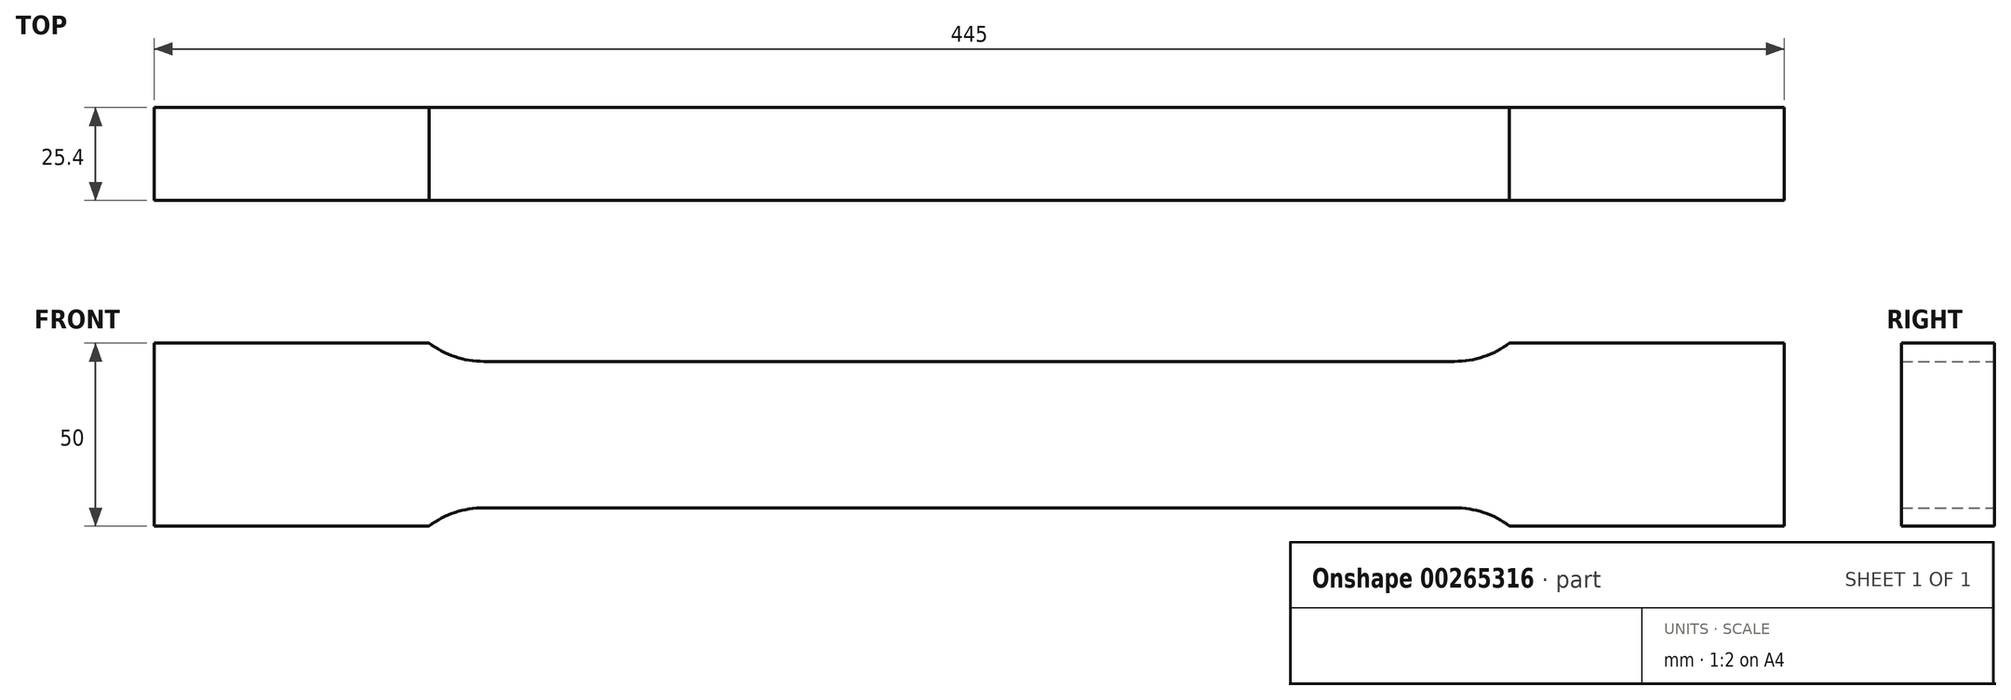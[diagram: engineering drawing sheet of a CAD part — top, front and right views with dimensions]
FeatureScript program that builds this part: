
annotation { "Feature Type Name" : "Feature", "Feature Type Description" : "" }
export const myFeature = defineFeature(function(context is Context, id is Id, definition is map)
    precondition{}
    {
        {
            var Q0;
            Q0=qCreatedBy(makeId("Front.planeOp"),FACE);
            var sketch = newSketch(context, id + "F0", { "sketchPlane" : qUnion([Q0])});
            skLineSegment(sketch, "E0", {"start": v(0, 20) * mm, "end": v(132.5, 20) * mm});
            skArc(sketch, "E1", {"start": v(132.5, 20) * mm, "mid": v(140.4, 21.28) * mm, "end": v(147.5, 25) * mm});
            skLineSegment(sketch, "E2", {"start": v(147.5, 25) * mm, "end": v(222.5, 25) * mm});
            skLineSegment(sketch, "E3", {"start": v(222.5, 25) * mm, "end": v(222.5, 0) * mm});
            skLineSegment(sketch, "E4.MirrorCS", {"start": v(0, -20) * mm, "end": v(132.5, -20) * mm});
            skLineSegment(sketch, "E5.MirrorCS", {"start": v(222.5, -25) * mm, "end": v(222.5, 0) * mm});
            skLineSegment(sketch, "E6.MirrorCS", {"start": v(147.5, -25) * mm, "end": v(222.5, -25) * mm});
            skArc(sketch, "E7.MirrorCS", {"start": v(132.5, -20) * mm, "mid": v(140.4, -21.28) * mm, "end": v(147.5, -25) * mm});
            skArc(sketch, "E8.MirrorCS", {"start": v(-132.5, -20) * mm, "mid": v(-140.4, -21.28) * mm, "end": v(-147.5, -25) * mm});
            skLineSegment(sketch, "E9.MirrorCS", {"start": v(-147.5, -25) * mm, "end": v(-222.5, -25) * mm});
            skArc(sketch, "E10.MirrorCS", {"start": v(-132.5, 20) * mm, "mid": v(-140.4, 21.28) * mm, "end": v(-147.5, 25) * mm});
            skLineSegment(sketch, "E11.MirrorCS", {"start": v(-147.5, 25) * mm, "end": v(-222.5, 25) * mm});
            skLineSegment(sketch, "E12.MirrorCS", {"start": v(-222.5, -25) * mm, "end": v(-222.5, 0) * mm});
            skLineSegment(sketch, "E13.MirrorCS", {"start": v(0, -20) * mm, "end": v(-132.5, -20) * mm});
            skLineSegment(sketch, "E14.MirrorCS", {"start": v(-222.5, 25) * mm, "end": v(-222.5, 0) * mm});
            skLineSegment(sketch, "E15.MirrorCS", {"start": v(0, 20) * mm, "end": v(-132.5, 20) * mm});
            skSolve(sketch);
        }
        {
            var Q0;
            Q0 = qSketchRegion(id + "F0", true);
            extrude(context, id + "F1", {"entities" : qUnion([Q0]), "endBound" : BoundingType.SYMMETRIC, "depth" : 25.4 * mm});
        }
    });
